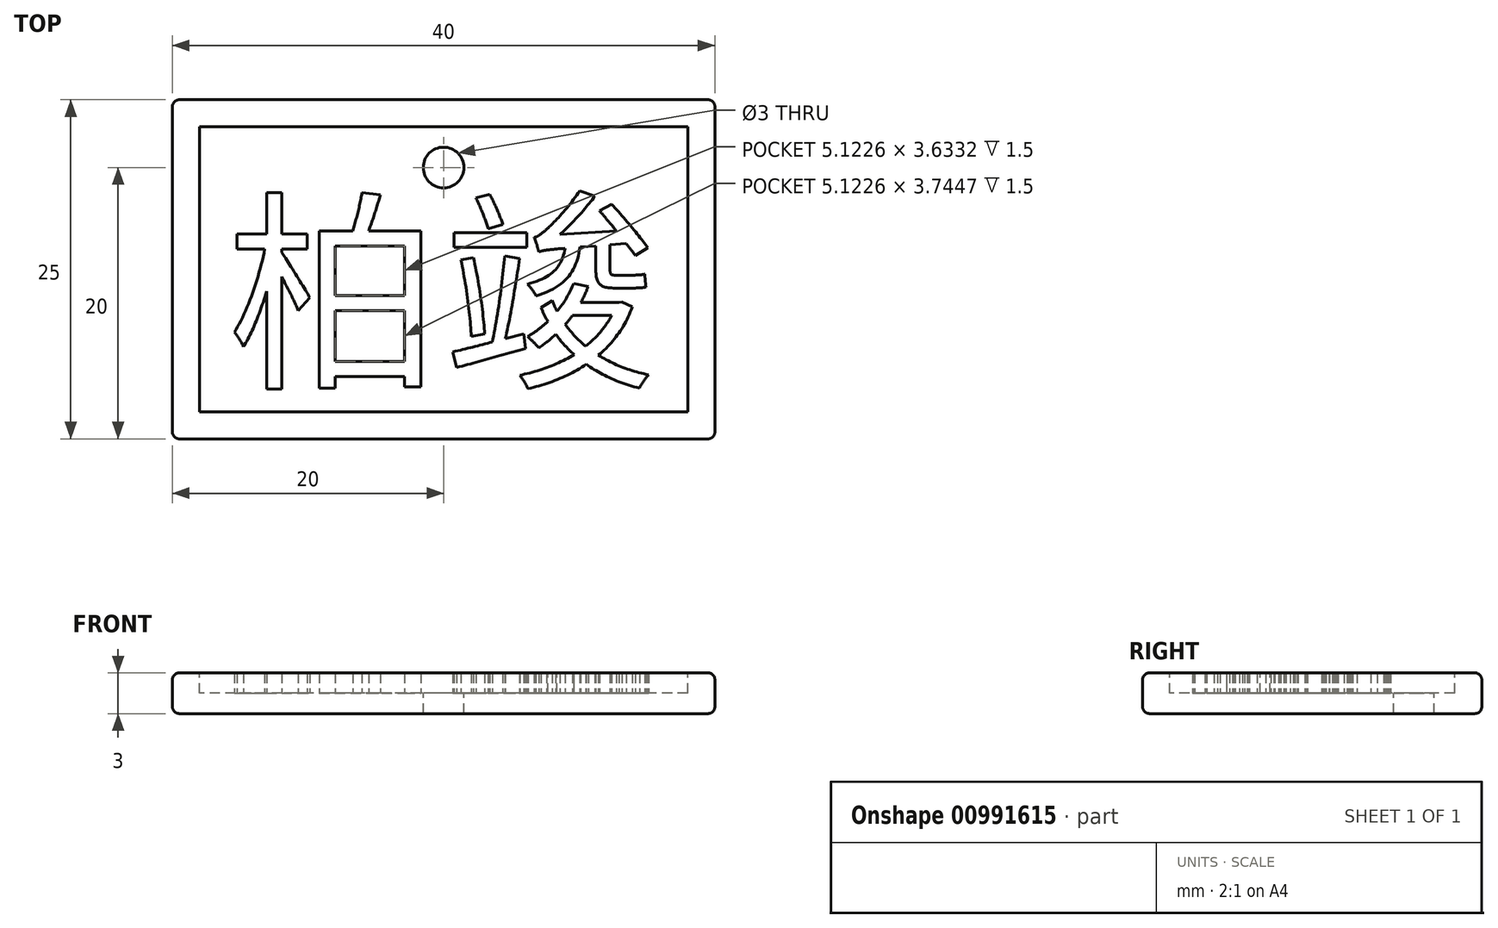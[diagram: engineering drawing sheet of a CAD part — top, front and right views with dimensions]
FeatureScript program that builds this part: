
annotation { "Feature Type Name" : "Feature", "Feature Type Description" : "" }
export const myFeature = defineFeature(function(context is Context, id is Id, definition is map)
    precondition{}
    {
        {
            var Q0;
            Q0=qCreatedBy(makeId("Top.planeOp"),FACE);
            var sketch = newSketch(context, id + "F0", { "sketchPlane" : qUnion([Q0])});
            skLineSegment(sketch, "E0.bottom", {"start": v(-20, 12.5) * mm, "end": v(20, 12.5) * mm});
            skLineSegment(sketch, "E0.top", {"start": v(-20, -12.5) * mm, "end": v(20, -12.5) * mm});
            skLineSegment(sketch, "E0.left", {"start": v(-20, 12.5) * mm, "end": v(-20, -12.5) * mm});
            skLineSegment(sketch, "E0.right", {"start": v(20, 12.5) * mm, "end": v(20, -12.5) * mm});
            skPoint(sketch, "E0.middle", {"position": v(0, 0) * mm});
            skSolve(sketch);
        }
        {
            var Q0;
            Q0 = qSketchRegion(id + "F0", true);
            extrude(context, id + "F1", {"entities" : qUnion([Q0]), "depth" : 3 * mm, "offsetDistance" : 25 * mm});
        }
        {
            var Q0;
            Q0=makeQuery(id+"F1.opExtrude","CAP_FACE",FACE,{"disambiguationData":[OSD([sQuery(id+"F0.wireOp",EDGE,"E0.bottom"),sQuery(id+"F0.wireOp",EDGE,"E0.top"),sQuery(id+"F0.wireOp",EDGE,"E0.left"),sQuery(id+"F0.wireOp",EDGE,"E0.right")])],"isStart":false});
            var sketch = newSketch(context, id + "F2", { "sketchPlane" : qUnion([Q0])});
            skLineSegment(sketch, "E1.0", {"start": v(-18, 10.5) * mm, "end": v(-18, -10.5) * mm});
            skLineSegment(sketch, "E1.1", {"start": v(18, 10.5) * mm, "end": v(-18, 10.5) * mm});
            skLineSegment(sketch, "E1.2", {"start": v(18, -10.5) * mm, "end": v(18, 10.5) * mm});
            skLineSegment(sketch, "E1.3", {"start": v(-18, -10.5) * mm, "end": v(18, -10.5) * mm});
            skSolve(sketch);
        }
        {
            var Q0;
            Q0 = qSketchRegion(id + "F2", true);
            extrude(context, id + "F3", {"entities" : qUnion([Q0]), "operationType" : NewBodyOperationType.REMOVE, "oppositeDirection" : true, "depth" : 1.5 * mm, "offsetDistance" : 25 * mm});
        }
        {
            var Q0;
            Q0=makeQuery(id+"F3.boolean.opBoolean","COPY",FACE,{"derivedFrom":makeQuery(id+"F3.opExtrude","CAP_FACE",FACE,{"disambiguationData":[OSD([sQuery(id+"F2.wireOp",EDGE,"E1.0"),sQuery(id+"F2.wireOp",EDGE,"E1.1"),sQuery(id+"F2.wireOp",EDGE,"E1.2"),sQuery(id+"F2.wireOp",EDGE,"E1.3")])],"isStart":false})});
            var sketch = newSketch(context, id + "F4", { "sketchPlane" : qUnion([Q0])});
            skCircle(sketch, "E2", {"center": v(0, 7.5) * mm, "radius": 1.5 * mm});
            skSolve(sketch);
        }
        {
            var Q0;
            Q0=makeQuery(id+"F4.imprint","IMPRINT",FACE,{"disambiguationData":[TD([[makeQuery(id+"F4.imprint","IMPRINT",EDGE,{"derivedFrom":sQuery(id+"F4.wireOp",EDGE,"E2")}),1.0]])]});
            extrude(context, id + "F5", {"entities" : qUnion([Q0]), "operationType" : NewBodyOperationType.REMOVE, "endBound" : BoundingType.THROUGH_ALL, "oppositeDirection" : true, "depth" : 25 * mm, "offsetDistance" : 25 * mm});
        }
        {
            var Q0;
            Q0=makeQuery(id+"F3.boolean.opBoolean","COPY",FACE,{"derivedFrom":makeQuery(id+"F3.opExtrude","CAP_FACE",FACE,{"disambiguationData":[OSD([sQuery(id+"F2.wireOp",EDGE,"E1.0"),sQuery(id+"F2.wireOp",EDGE,"E1.1"),sQuery(id+"F2.wireOp",EDGE,"E1.2"),sQuery(id+"F2.wireOp",EDGE,"E1.3")])],"isStart":false})});
            var sketch = newSketch(context, id + "F6", { "sketchPlane" : qUnion([Q0])});
            skText(sketch, "E3", { "text": "柏竣", "fontName": "NotoSansCJKtc-Regular.otf"});
            skPoint(sketch, "E4", {"position": v(0, -1.89) * mm});
            const initialGuessF6  = {"E3": [-0.016, -0.0076, 1, 0, 0.01142]};
            skSetInitialGuess(sketch, initialGuessF6);
            skSolve(sketch);
        }
        {
            var Q0;
            Q0 = qSketchRegion(id + "F6", true);
            extrude(context, id + "F7", {"entities" : qUnion([Q0]), "operationType" : NewBodyOperationType.ADD, "depth" : 1.5 * mm, "offsetDistance" : 25 * mm});
        }
        {
            var Q0;
            Q0=makeQuery(id+"F1.opExtrude","SWEPT_FACE",FACE,{"disambiguationData":[OSD([sQuery(id+"F0.wireOp",EDGE,"E0.top")])]});
            var Q1;
            Q1=makeQuery(id+"F1.opExtrude","SWEPT_FACE",FACE,{"disambiguationData":[OSD([sQuery(id+"F0.wireOp",EDGE,"E0.left")])]});
            var Q2;
            Q2=makeQuery(id+"F1.opExtrude","SWEPT_FACE",FACE,{"disambiguationData":[OSD([sQuery(id+"F0.wireOp",EDGE,"E0.right")])]});
            var Q3;
            Q3=makeQuery(id+"F1.opExtrude","SWEPT_FACE",FACE,{"disambiguationData":[OSD([sQuery(id+"F0.wireOp",EDGE,"E0.bottom")])]});
            fillet(context, id + "F8", {"entities" : qUnion([Q0, Q1, Q2, Q3]), "radius" : 0.5 * mm, "tangentPropagation" : true, "allowEdgeOverflow" : false});
        }
    });
